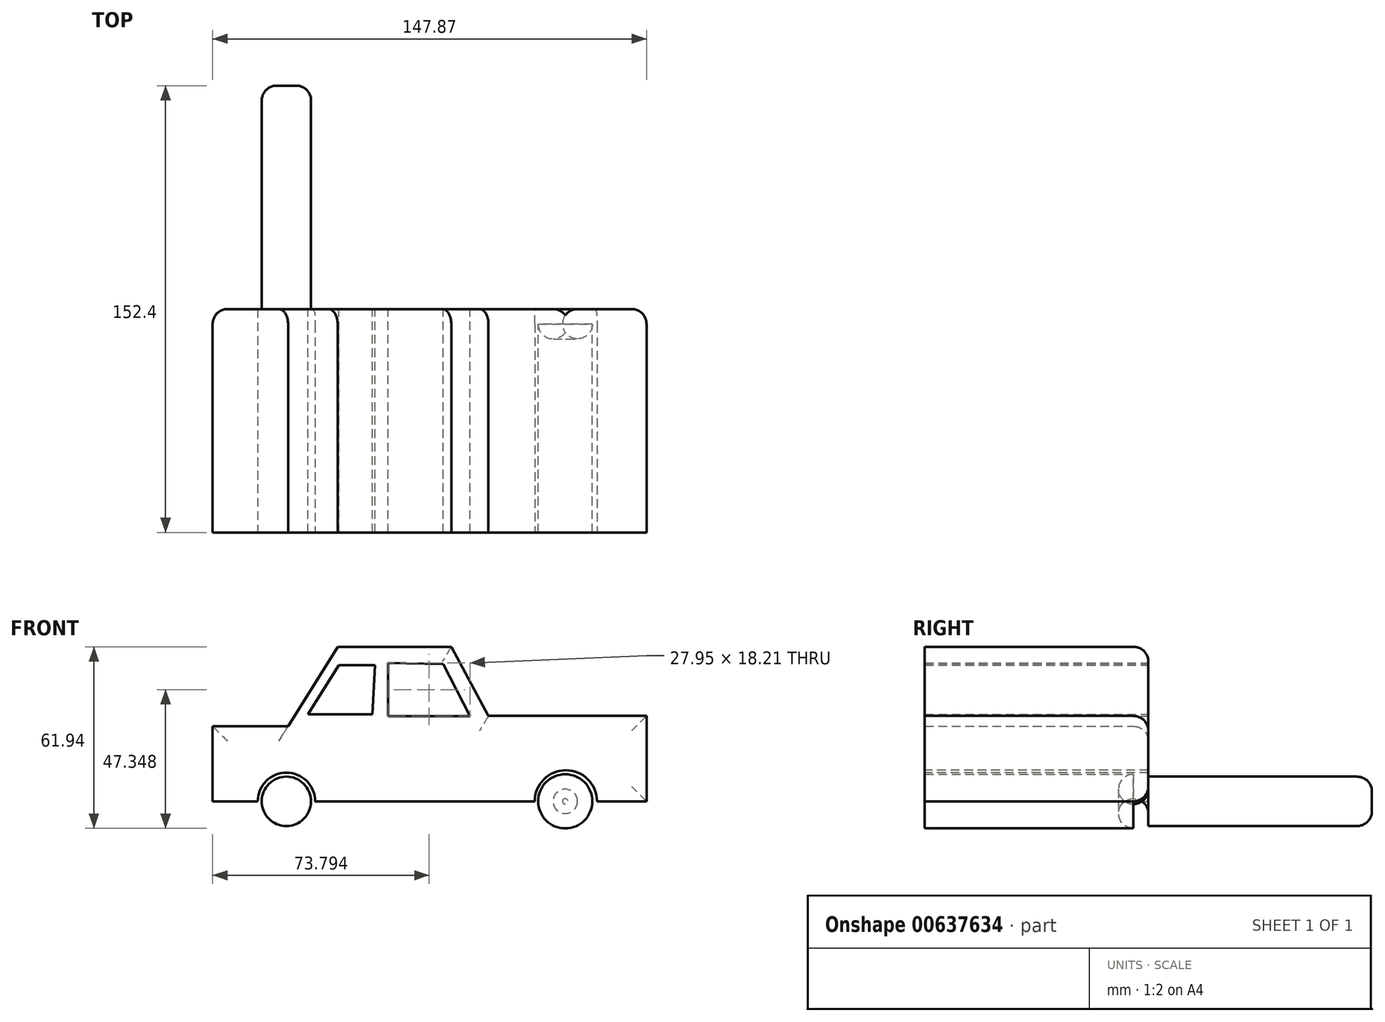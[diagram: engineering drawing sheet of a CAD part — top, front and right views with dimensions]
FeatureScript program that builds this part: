
annotation { "Feature Type Name" : "Feature", "Feature Type Description" : "" }
export const myFeature = defineFeature(function(context is Context, id is Id, definition is map)
    precondition{}
    {
        {
            var Q0;
            Q0=qCreatedBy(makeId("Front.planeOp"),FACE);
            var sketch = newSketch(context, id + "F0", { "sketchPlane" : qUnion([Q0])});
            skLineSegment(sketch, "E0", {"start": v(-59.82, 0) * mm, "end": v(-59.82, 25.6) * mm});
            skLineSegment(sketch, "E1", {"start": v(-59.82, 25.6) * mm, "end": v(-34.12, 25.6) * mm});
            skLineSegment(sketch, "E2", {"start": v(-34.12, 25.6) * mm, "end": v(-17.22, 52.71) * mm});
            skLineSegment(sketch, "E3", {"start": v(-17.22, 52.71) * mm, "end": v(21.5, 52.71) * mm});
            skLineSegment(sketch, "E4", {"start": v(21.5, 52.71) * mm, "end": v(34.18, 29.13) * mm});
            skLineSegment(sketch, "E5", {"start": v(34.18, 29.13) * mm, "end": v(88.05, 29.13) * mm});
            skLineSegment(sketch, "E6", {"start": v(88.05, 29.13) * mm, "end": v(88.05, 0) * mm});
            skLineSegment(sketch, "E7", {"start": v(88.05, 0) * mm, "end": v(-59.82, 0) * mm});
            skSolve(sketch);
        }
        {
            var Q0;
            Q0 = qSketchRegion(id + "F0", true);
            extrude(context, id + "F1", {"entities" : qUnion([Q0]), "depth" : 76.2 * mm, "offsetDistance" : 25.4 * mm});
        }
        {
            var Q0;
            Q0=makeQuery(id+"F1.opExtrude","CAP_FACE",FACE,{"disambiguationData":[OSD([sQuery(id+"F0.wireOp",EDGE,"E0"),sQuery(id+"F0.wireOp",EDGE,"E1"),sQuery(id+"F0.wireOp",EDGE,"E2"),sQuery(id+"F0.wireOp",EDGE,"E3"),sQuery(id+"F0.wireOp",EDGE,"E4"),sQuery(id+"F0.wireOp",EDGE,"E5"),sQuery(id+"F0.wireOp",EDGE,"E6"),sQuery(id+"F0.wireOp",EDGE,"E7")])],"isStart":false});
            var sketch = newSketch(context, id + "F2", { "sketchPlane" : qUnion([Q0])});
            skCircle(sketch, "E8", {"center": v(60.57, 0) * mm, "radius": 10.6 * mm});
            skSolve(sketch);
        }
        {
            var Q0;
            Q0 = qSketchRegion(id + "F2", true);
            extrude(context, id + "F3", {"entities" : qUnion([Q0]), "operationType" : NewBodyOperationType.REMOVE, "oppositeDirection" : true, "depth" : 76.2 * mm, "offsetDistance" : 25.4 * mm});
        }
        {
            var Q0;
            Q0=makeQuery(id+"F1.opExtrude","CAP_FACE",FACE,{"disambiguationData":[OSD([sQuery(id+"F0.wireOp",EDGE,"E0"),sQuery(id+"F0.wireOp",EDGE,"E1"),sQuery(id+"F0.wireOp",EDGE,"E2"),sQuery(id+"F0.wireOp",EDGE,"E3"),sQuery(id+"F0.wireOp",EDGE,"E4"),sQuery(id+"F0.wireOp",EDGE,"E5"),sQuery(id+"F0.wireOp",EDGE,"E6"),sQuery(id+"F0.wireOp",EDGE,"E7")])],"isStart":false});
            var sketch = newSketch(context, id + "F4", { "sketchPlane" : qUnion([Q0])});
            skCircle(sketch, "E9", {"center": v(-34.68, 0) * mm, "radius": 9.77 * mm});
            skSolve(sketch);
        }
        {
            var Q0;
            Q0 = qSketchRegion(id + "F4", true);
            extrude(context, id + "F5", {"entities" : qUnion([Q0]), "operationType" : NewBodyOperationType.REMOVE, "oppositeDirection" : true, "depth" : 76.2 * mm, "offsetDistance" : 25.4 * mm});
        }
        {
            var Q0;
            Q0=makeQuery(id+"F1.opExtrude","CAP_FACE",FACE,{"disambiguationData":[OSD([sQuery(id+"F0.wireOp",EDGE,"E0"),sQuery(id+"F0.wireOp",EDGE,"E1"),sQuery(id+"F0.wireOp",EDGE,"E2"),sQuery(id+"F0.wireOp",EDGE,"E3"),sQuery(id+"F0.wireOp",EDGE,"E4"),sQuery(id+"F0.wireOp",EDGE,"E5"),sQuery(id+"F0.wireOp",EDGE,"E6"),sQuery(id+"F0.wireOp",EDGE,"E7")])],"isStart":true});
            var sketch = newSketch(context, id + "F6", { "sketchPlane" : qUnion([Q0])});
            skLineSegment(sketch, "E10", {"start": v(-18.74, 46.8) * mm, "end": v(-27.95, 29.01) * mm});
            skLineSegment(sketch, "E11", {"start": v(-27.95, 29.01) * mm, "end": v(0, 29.01) * mm});
            skLineSegment(sketch, "E12", {"start": v(0, 29.01) * mm, "end": v(0, 47.22) * mm});
            skLineSegment(sketch, "E13", {"start": v(0, 47.22) * mm, "end": v(-18.74, 46.8) * mm});
            skSolve(sketch);
        }
        {
            var Q0;
            Q0 = qSketchRegion(id + "F6", true);
            extrude(context, id + "F7", {"entities" : qUnion([Q0]), "operationType" : NewBodyOperationType.REMOVE, "oppositeDirection" : true, "depth" : 76.2 * mm, "offsetDistance" : 25.4 * mm});
        }
        {
            var Q0;
            Q0=makeQuery(id+"F1.opExtrude","CAP_FACE",FACE,{"disambiguationData":[OSD([sQuery(id+"F0.wireOp",EDGE,"E0"),sQuery(id+"F0.wireOp",EDGE,"E1"),sQuery(id+"F0.wireOp",EDGE,"E2"),sQuery(id+"F0.wireOp",EDGE,"E3"),sQuery(id+"F0.wireOp",EDGE,"E4"),sQuery(id+"F0.wireOp",EDGE,"E5"),sQuery(id+"F0.wireOp",EDGE,"E6"),sQuery(id+"F0.wireOp",EDGE,"E7")])],"isStart":true});
            var sketch = newSketch(context, id + "F8", { "sketchPlane" : qUnion([Q0])});
            skLineSegment(sketch, "E14", {"start": v(4.5, 46.39) * mm, "end": v(16.85, 46.39) * mm});
            skLineSegment(sketch, "E15", {"start": v(16.85, 46.39) * mm, "end": v(27.32, 29.64) * mm});
            skLineSegment(sketch, "E16", {"start": v(27.32, 29.64) * mm, "end": v(5.34, 29.64) * mm});
            skLineSegment(sketch, "E17", {"start": v(5.34, 29.64) * mm, "end": v(4.5, 46.39) * mm});
            skSolve(sketch);
        }
        {
            var Q0;
            Q0 = qSketchRegion(id + "F8", true);
            extrude(context, id + "F9", {"entities" : qUnion([Q0]), "operationType" : NewBodyOperationType.REMOVE, "depth" : 76.2 * mm, "offsetDistance" : 25.4 * mm});
        }
        {
            var Q0;
            Q0 = qSketchRegion(id + "F8", true);
            extrude(context, id + "F10", {"entities" : qUnion([Q0]), "operationType" : NewBodyOperationType.REMOVE, "oppositeDirection" : true, "depth" : 76.2 * mm, "offsetDistance" : 25.4 * mm});
        }
        {
            var Q0;
            Q0=qCreatedBy(makeId("Front.planeOp"),FACE);
            var sketch = newSketch(context, id + "F11", { "sketchPlane" : qUnion([Q0])});
            skCircle(sketch, "E18", {"center": v(60.35, 0) * mm, "radius": 9.23 * mm});
            skSolve(sketch);
        }
        {
            var Q0;
            Q0 = qSketchRegion(id + "F11", true);
            extrude(context, id + "F12", {"entities" : qUnion([Q0]), "depth" : 76.2 * mm, "offsetDistance" : 25.4 * mm});
        }
        {
            var Q0;
            Q0=makeQuery(id+"F1.opExtrude","CAP_FACE",FACE,{"disambiguationData":[OSD([sQuery(id+"F0.wireOp",EDGE,"E0"),sQuery(id+"F0.wireOp",EDGE,"E1"),sQuery(id+"F0.wireOp",EDGE,"E2"),sQuery(id+"F0.wireOp",EDGE,"E3"),sQuery(id+"F0.wireOp",EDGE,"E4"),sQuery(id+"F0.wireOp",EDGE,"E5"),sQuery(id+"F0.wireOp",EDGE,"E6"),sQuery(id+"F0.wireOp",EDGE,"E7")])],"isStart":true});
            var sketch = newSketch(context, id + "F13", { "sketchPlane" : qUnion([Q0])});
            skCircle(sketch, "E19", {"center": v(34.68, 0) * mm, "radius": 8.4 * mm});
            skSolve(sketch);
        }
        {
            var Q0;
            Q0 = qSketchRegion(id + "F13", true);
            extrude(context, id + "F14", {"entities" : qUnion([Q0]), "depth" : 76.2 * mm, "offsetDistance" : 25.4 * mm});
        }
        {
            var Q0;
            Q0=makeQuery(id+"F1.opExtrude","CAP_EDGE",EDGE,{"disambiguationData":[OSD([sQuery(id+"F0.wireOp",EDGE,"E6")])],"isStart":true});
            var Q1;
            {var subQ0=sQuery(id+"F0.wireOp",EDGE,"E7");var subQ1=sQuery(id+"F0.wireOp",EDGE,"E6");Q1=makeQuery(id+"F3.boolean.opBoolean","SPLIT",EDGE,{"disambiguationData":[TD([makeQuery(id+"F1.opExtrude","SWEPT_FACE",FACE,{"disambiguationData":[OSD([subQ1])]})])],"derivedFrom":makeQuery(id+"F1.opExtrude","CAP_EDGE",EDGE,{"disambiguationData":[OSD([subQ0])],"isStart":true})});}
            var Q2;
            Q2=makeQuery(id+"F3.boolean.opBoolean","COPY",EDGE,{"derivedFrom":makeQuery(id+"F3.opExtrude","CAP_EDGE",EDGE,{"disambiguationData":[OSD([sQuery(id+"F2.wireOp",EDGE,"E8")])],"isStart":false})});
            var Q3;
            Q3=makeQuery(id+"F12.opExtrude","CAP_FACE",FACE,{"disambiguationData":[OSD([sQuery(id+"F11.wireOp",EDGE,"E18")])],"isStart":true});
            var Q4;
            {var subQ0=sQuery(id+"F0.wireOp",EDGE,"E7");var subQ1=sQuery(id+"F0.wireOp",EDGE,"E0");var subQ4=makeQuery(id+"F3.opExtrude","SWEPT_FACE",FACE,{"disambiguationData":[OSD([sQuery(id+"F2.wireOp",EDGE,"E8")])]});Q4=makeQuery(id+"F5.boolean.opBoolean","SPLIT",EDGE,{"disambiguationData":[TD([makeQuery(id+"F3.boolean.opBoolean","COPY",FACE,{"derivedFrom":subQ4})])],"derivedFrom":makeQuery(id+"F3.boolean.opBoolean","SPLIT",EDGE,{"disambiguationData":[TD([makeQuery(id+"F1.opExtrude","SWEPT_FACE",FACE,{"disambiguationData":[OSD([subQ1])]})])],"derivedFrom":makeQuery(id+"F1.opExtrude","CAP_EDGE",EDGE,{"disambiguationData":[OSD([subQ0])],"isStart":true})})});}
            var Q5;
            Q5=makeQuery(id+"F1.opExtrude","CAP_EDGE",EDGE,{"disambiguationData":[OSD([sQuery(id+"F0.wireOp",EDGE,"E5")])],"isStart":true});
            var Q6;
            Q6=makeQuery(id+"F1.opExtrude","CAP_EDGE",EDGE,{"disambiguationData":[OSD([sQuery(id+"F0.wireOp",EDGE,"E4")])],"isStart":true});
            var Q7;
            Q7=makeQuery(id+"F1.opExtrude","CAP_EDGE",EDGE,{"disambiguationData":[OSD([sQuery(id+"F0.wireOp",EDGE,"E3")])],"isStart":true});
            var Q8;
            Q8=makeQuery(id+"F1.opExtrude","CAP_EDGE",EDGE,{"disambiguationData":[OSD([sQuery(id+"F0.wireOp",EDGE,"E1")])],"isStart":true});
            var Q9;
            Q9=makeQuery(id+"F1.opExtrude","CAP_EDGE",EDGE,{"disambiguationData":[OSD([sQuery(id+"F0.wireOp",EDGE,"E0")])],"isStart":true});
            var Q10;
            Q10=makeQuery(id+"F14.opExtrude","CAP_FACE",FACE,{"disambiguationData":[OSD([sQuery(id+"F13.wireOp",EDGE,"E19")])],"isStart":false});
            var Q11;
            Q11=makeQuery(id+"F5.boolean.opBoolean","COPY",EDGE,{"derivedFrom":makeQuery(id+"F5.opExtrude","CAP_EDGE",EDGE,{"disambiguationData":[OSD([sQuery(id+"F4.wireOp",EDGE,"E9")])],"isStart":false})});
            var Q12;
            Q12=makeQuery(id+"F10.boolean.opBoolean","COPY",EDGE,{"derivedFrom":makeQuery(id+"F10.opExtrude","CAP_EDGE",EDGE,{"disambiguationData":[OSD([sQuery(id+"F8.wireOp",EDGE,"E16")])],"isStart":true})});
            var Q13;
            Q13=makeQuery(id+"F7.boolean.opBoolean","COPY",EDGE,{"derivedFrom":makeQuery(id+"F7.opExtrude","CAP_EDGE",EDGE,{"disambiguationData":[OSD([sQuery(id+"F6.wireOp",EDGE,"E11")])],"isStart":true})});
            var Q14;
            Q14=makeQuery(id+"F7.boolean.opBoolean","COPY",EDGE,{"derivedFrom":makeQuery(id+"F7.opExtrude","CAP_EDGE",EDGE,{"disambiguationData":[OSD([sQuery(id+"F6.wireOp",EDGE,"E10")])],"isStart":true})});
            var Q15;
            Q15=makeQuery(id+"F7.boolean.opBoolean","COPY",EDGE,{"derivedFrom":makeQuery(id+"F7.opExtrude","CAP_EDGE",EDGE,{"disambiguationData":[OSD([sQuery(id+"F6.wireOp",EDGE,"E13")])],"isStart":true})});
            fillet(context, id + "F15", {"entities" : qUnion([Q0, Q1, Q2, Q3, Q4, Q5, Q6, Q7, Q8, Q9, Q10, Q11, Q12, Q13, Q14, Q15]), "radius" : 5.08 * mm, "tangentPropagation" : true, "allowEdgeOverflow" : false});
        }
    });
